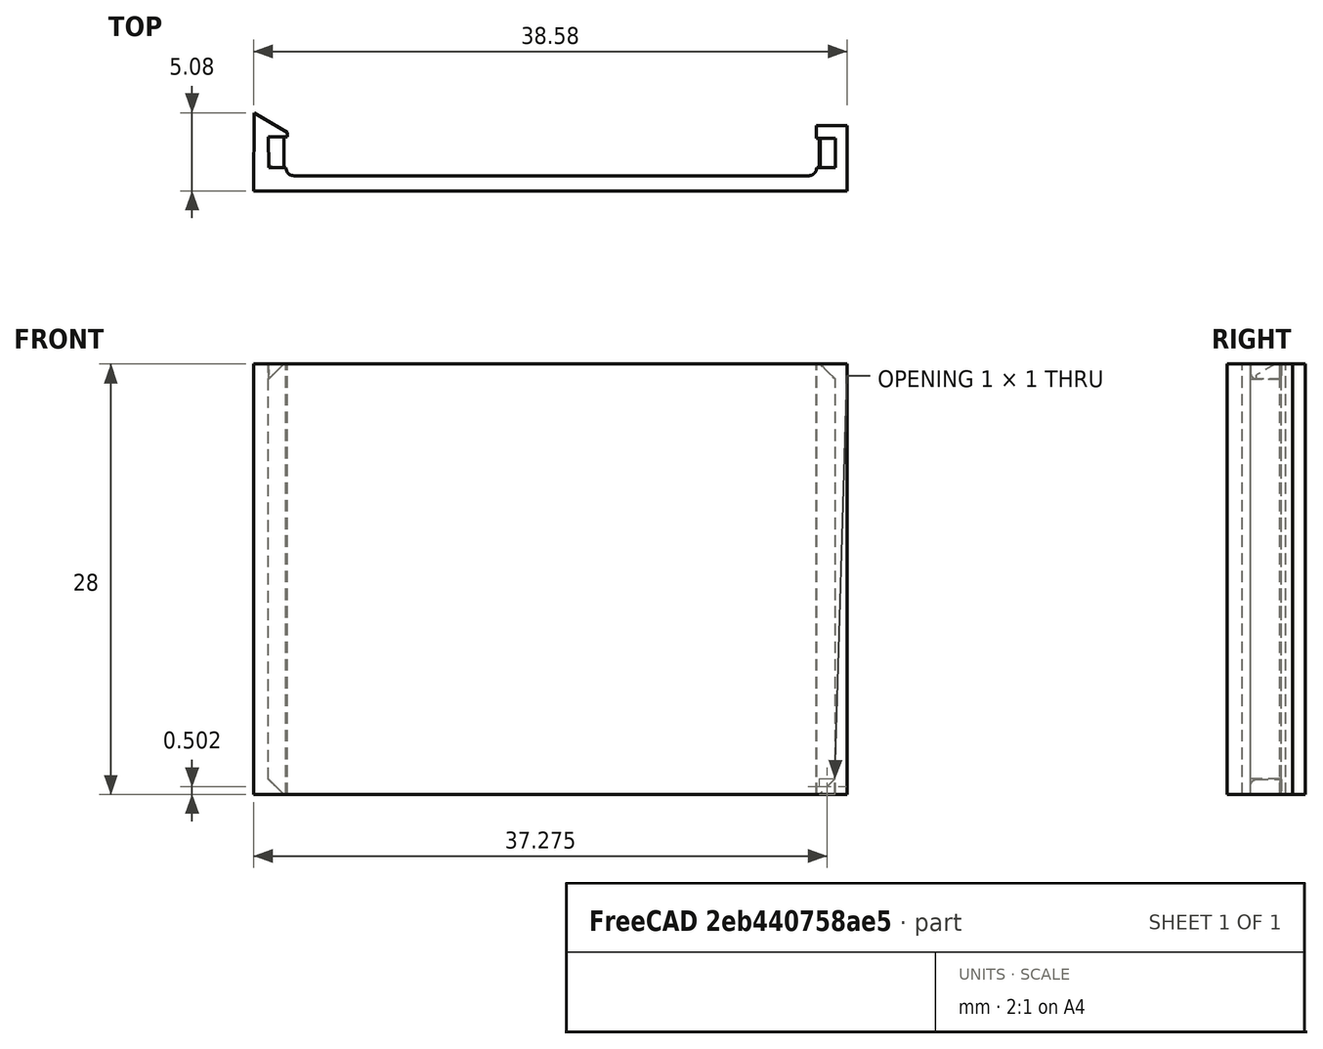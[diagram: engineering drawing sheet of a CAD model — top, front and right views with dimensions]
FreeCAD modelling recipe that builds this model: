
FCSTD DOCUMENT  (FreeCAD 0.18.4R)
Label: GPSBoardClip
License: All rights reserved
LicenseURL: http://en.wikipedia.org/wiki/All_rights_reserved
objects: Sketcher::SketchObject×5, PartDesign::Pad×5, Part::Fillet×3, Part::MultiFuse×1, Mesh::Feature×1
note: 19 computed .brp shape members not serialized (recipe doc carries the construction recipe); baked Part::Feature solids carry a one-line shape summary decoded from their .brp

FEATURE [Sketcher::SketchObject] Sketch
  MapMode = 5
  sketch-geometry (16):
    g0: LineSegment StartX=-17.4674 StartY=-7.02844 StartZ=0 EndX=17.02 EndY=-7.02844 EndZ=0
    g1: LineSegment StartX=18.9972 StartY=-8.01786 StartZ=0 EndX=-19.5785 EndY=-8.01786 EndZ=0
    g2: LineSegment StartX=-17.4674 StartY=-6.49011 StartZ=0 EndX=-17.4674 EndY=-7.02844 EndZ=0
    g3: LineSegment StartX=19.0009 StartY=-3.77022 StartZ=0 EndX=18.9972 EndY=-8.01786 EndZ=0
    g4: LineSegment StartX=16.9998 StartY=-3.76858 StartZ=0 EndX=17.0033 EndY=-4.58507 EndZ=0
    g5: LineSegment StartX=16.9998 StartY=-3.76858 StartZ=0 EndX=19.0009 EndY=-3.77022 EndZ=0
    g6: LineSegment StartX=17.0033 StartY=-4.58507 StartZ=0 EndX=18.2249 EndY=-4.58482 EndZ=0
    g7: LineSegment StartX=18.2249 StartY=-4.58482 StartZ=0 EndX=18.227 EndY=-6.4933 EndZ=0
    g8: LineSegment StartX=18.227 StartY=-6.4933 StartZ=0 EndX=17.0164 EndY=-6.4933 EndZ=0
    g9: LineSegment StartX=17.0164 StartY=-6.4933 StartZ=0 EndX=17.02 EndY=-7.02844 EndZ=0
    g10: LineSegment StartX=-17.4674 StartY=-6.49011 StartZ=0 EndX=-18.6023 EndY=-6.49011 EndZ=0
    g11: LineSegment StartX=-18.6023 StartY=-6.49011 StartZ=0 EndX=-18.6091 EndY=-4.50157 EndZ=0
    g12: LineSegment StartX=-18.6091 StartY=-4.50157 StartZ=0 EndX=-17.3894 EndY=-4.5012 EndZ=0
    g13: LineSegment StartX=-17.3894 StartY=-4.5012 StartZ=0 EndX=-17.3861 EndY=-4.20382 EndZ=0
    g14: LineSegment StartX=-17.3861 StartY=-4.20382 StartZ=0 EndX=-19.5501 EndY=-2.94122 EndZ=0
    g15: LineSegment StartX=-19.5501 StartY=-2.94122 StartZ=0 EndX=-19.5785 EndY=-8.01786 EndZ=0
  constraints (19):
    c: Horizontal(g0)
    c: Horizontal(g1)
    c: Vertical(g2)
    c: Coincident(g1,g3)
    c: Coincident(g5,g4)
    c: Coincident(g4,g6)
    c: Coincident(g6,g7)
    c: Coincident(g7,g8)
    c: Coincident(g0,g9)
    c: Coincident(g9,g8)
    c: Coincident(g5,g3)
    c: Coincident(g10,g2)
    c: Coincident(g10,g11)
    c: Coincident(g11,g12)
    c: Coincident(g12,g13)
    c: Coincident(g13,g14)
    c: Coincident(g2,g0)
    c: Coincident(g15,g14)
    c: Coincident(g15,g1)
FEATURE [PartDesign::Pad] Pad
  Length = 28
  Length2 = 100
  Profile = -> Sketch
  Type = 0
FEATURE [Sketcher::SketchObject] Sketch004
  MapMode = 5
  Placement = pos=(-11.64,-4.5,6.03) rot=(1,0,0;1.5708rad)
  sketch-geometry (3):
    g0: LineSegment StartX=-7.00166 StartY=-5.01077 StartZ=0 EndX=-6.98953 EndY=-6.02972 EndZ=0
    g1: LineSegment StartX=-6.98953 StartY=-6.02972 StartZ=0 EndX=-5.96627 EndY=-6.02972 EndZ=0
    g2: LineSegment StartX=-7.00166 StartY=-5.01077 StartZ=0 EndX=-5.96627 EndY=-6.02972 EndZ=0
  constraints (3):
    c: Coincident(g0,g1)
    c: Coincident(g2,g0)
    c: Coincident(g2,g1)
FEATURE [PartDesign::Pad] Pad004  label="stopper002"
  Length = 2.2
  Length2 = 100
  Placement = pos=(-11.64,-4.5,6.03) rot=(1,0,0;1.5708rad)
  Profile = -> Sketch004
  Type = 0
FEATURE [Sketcher::SketchObject] Sketch006
  MapMode = 5
  Placement = pos=(18.2,-4.5,0.03) rot=(1,0,0;1.5708rad)
  sketch-geometry (3):
    g0: LineSegment StartX=-0.005347 StartY=0.971544 StartZ=0 EndX=-0.005347 EndY=-0.027131 EndZ=0
    g1: LineSegment StartX=-0.005347 StartY=-0.027131 StartZ=0 EndX=-1.00402 EndY=-0.027124 EndZ=0
    g2: LineSegment StartX=-1.00402 StartY=-0.027124 StartZ=0 EndX=-0.005347 EndY=0.971544 EndZ=0
  constraints (3):
    c: Coincident(g0,g1)
    c: Coincident(g1,g2)
    c: Coincident(g2,g0)
FEATURE [PartDesign::Pad] Pad006  label="stopper003"
  Length = 2.2
  Length2 = 100
  Placement = pos=(18.2,-4.5,0.03) rot=(1,0,0;1.5708rad)
  Profile = -> Sketch006
  Type = 0
FEATURE [Sketcher::SketchObject] Sketch007
  MapMode = 5
  Placement = pos=(18.25,-4.5,27.02) rot=(1,0,0;1.5708rad)
  sketch-geometry (3):
    g0: LineSegment StartX=-0.005347 StartY=0.971544 StartZ=0 EndX=-0.005347 EndY=-0.027131 EndZ=0
    g1: LineSegment StartX=-0.005347 StartY=-0.027131 StartZ=0 EndX=-1.00779 EndY=0.969763 EndZ=0
    g2: LineSegment StartX=-1.00779 StartY=0.969763 StartZ=0 EndX=-0.005347 EndY=0.971544 EndZ=0
  constraints (3):
    c: Coincident(g0,g1)
    c: Coincident(g1,g2)
    c: Coincident(g2,g0)
FEATURE [PartDesign::Pad] Pad007  label="stopper004"
  Length = 2.2
  Length2 = 100
  Placement = pos=(18.25,-4.5,27.02) rot=(1,0,0;1.5708rad)
  Profile = -> Sketch007
  Type = 0
FEATURE [Sketcher::SketchObject] Sketch008
  MapMode = 5
  Placement = pos=(-17.6,-4.5,27.02) rot=(1,0,0;1.5708rad)
  sketch-geometry (3):
    g0: LineSegment StartX=-0.005347 StartY=0.971544 StartZ=0 EndX=-1.00207 EndY=-0.002707 EndZ=0
    g1: LineSegment StartX=-1.00207 StartY=-0.002707 StartZ=0 EndX=-1.00779 EndY=0.969763 EndZ=0
    g2: LineSegment StartX=-1.00779 StartY=0.969763 StartZ=0 EndX=-0.005347 EndY=0.971544 EndZ=0
  constraints (3):
    c: Coincident(g0,g1)
    c: Coincident(g1,g2)
    c: Coincident(g2,g0)
FEATURE [PartDesign::Pad] Pad008  label="stopper001"
  Length = 2.2
  Length2 = 100
  Placement = pos=(-17.6,-4.5,27.02) rot=(1,0,0;1.5708rad)
  Profile = -> Sketch008
  Type = 0
FEATURE [Part::MultiFuse] Fusion
  Shapes = -> [Pad,Pad004,Pad006,Pad007,Pad008]
FEATURE [Part::Fillet] Fillet
  Base = -> Fusion
  Edges = 1 edges r=0.5: [Edge15]
FEATURE [Part::Fillet] Fillet001
  Base = -> Fillet
  Edges = 1 edges r=0.5: [Edge3]
FEATURE [Part::Fillet] Fillet002
  Base = -> Fillet001
  Edges = 1 edges r=0.4: [Edge46]
FEATURE [Mesh::Feature] Mesh  label="Fillet002 (Meshed)"
